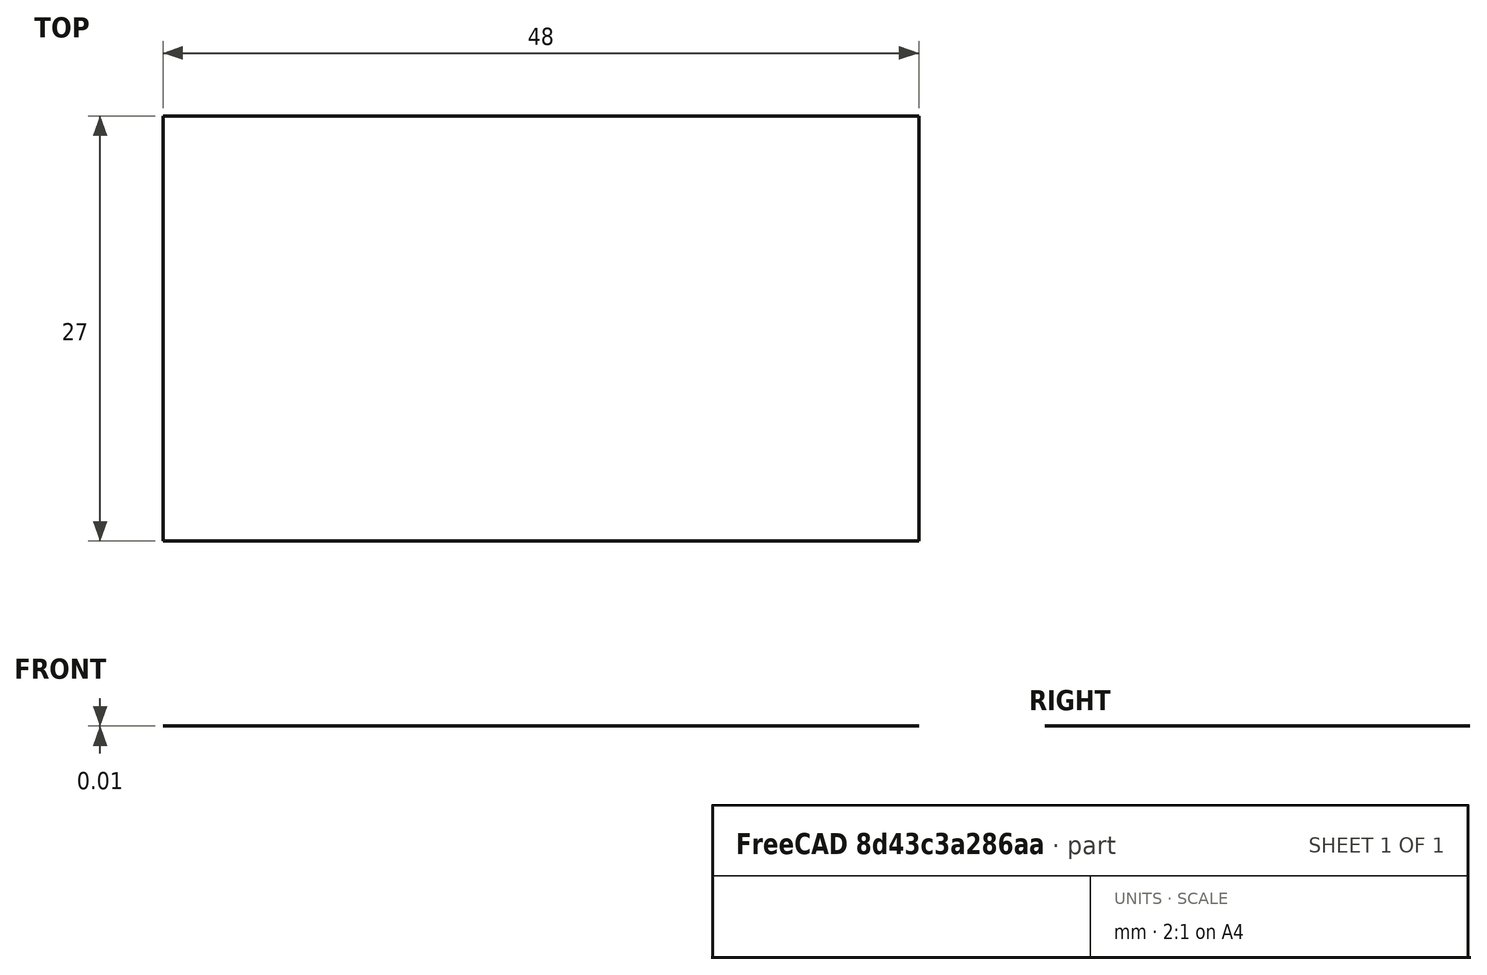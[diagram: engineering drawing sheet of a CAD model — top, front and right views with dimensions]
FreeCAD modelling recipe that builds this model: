
FCSTD DOCUMENT  (FreeCAD 0.19R23058 (Git))
Label: label_3
License: All rights reserved
LicenseURL: http://en.wikipedia.org/wiki/All_rights_reserved
objects: App::MaterialObjectPython×1, Part::Box×1, App::DocumentObjectGroupPython×1, App::FeaturePython×1
note: 1 computed .brp shape members not serialized (recipe doc carries the construction recipe); baked Part::Feature solids carry a one-line shape summary decoded from their .brp

FEATURE [App::MaterialObjectPython] Material  label="Label"  # material (typed FeaturePython)
  Description = This is a blend AcrylnitrilButadienStyrol (ABS) material card. The values are at the low end of the spectrum. If you need a more precise material definition use the more specialised ABS-blend cards.
  Material = AuthorAndLicense=ABS-Generic,CardName=ABS-Generic,Color=(0.8, 0.8, 0.8, 1.0),Density=1060 kg/m^3,+16 more (map truncated)
  ProductURL = https://en.wikipedia.org/wiki/Acrylonitrile_butadiene_styrene
  Transparency = 0
FEATURE [Part::Box] Box  label="Куб"
  AttacherType = Attacher::AttachEngine3D
  Height = 0.01
  Length = 48
  Material = -> Material
  Width = 27
FEATURE [App::DocumentObjectGroupPython] MaterialContainer  label="Materials"  # scripted group (container) (typed FeaturePython)
  Group = -> [Material]
FEATURE [App::FeaturePython] TextureConfig  # WARN: FeaturePython — macro-defined, semantics opaque (R4)
